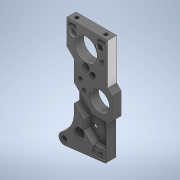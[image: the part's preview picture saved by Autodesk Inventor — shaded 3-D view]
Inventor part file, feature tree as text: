
AUTODESK INVENTOR PART (.ipt)
format: ipt  version: 2022 (Build 260153000, 153)  size: 579,072 bytes
history: native  units: mm
features: extrude x16, sketch x11, fillet x5, projected_geometry x5, thread x2, chamfer x1
ambient origin geometry x8: Origin, YZ Plane, XZ Plane, XY Plane, X Axis, Y Axis, Z Axis, Center Point
bodies: Solid1 (feature_tree)
feature tree (40):
  extrude  "Extrusion1"  Depth=6.0mm
  fillet  "Fillet1"  Radius=23.5mm
  fillet  "Fillet2"  Radius=6.0mm
  extrude  "Extrusion2"  Depth=3.0mm
  extrude  "Extrusion3"  Depth=56.0mm
  thread  "Thread1"  [1 undecoded]
  thread  "Thread2"  [1 undecoded]
  sketch  "Sketch5"  dims[d4=0.0mm d5=3.0mm]
  extrude  "Extrusion4"  Depth=12.5mm
  extrude  "Extrusion5"  Depth=2.1mm
  extrude  "Extrusion6"  Depth=4.0mm
  extrude  "Extrusion7"  TaperAngle=45.0deg  [1 undecoded]
  extrude  "Extrusion8"  Depth=12.0mm
  extrude  "Extrusion9"  TaperAngle=135.0deg  [1 undecoded]
  extrude  "Extrusion10"  Depth=5.0mm TaperAngle=0.0deg
  fillet  "Fillet3"  Radius=3.0mm
  extrude  "Extrusion11"  Depth=10.0mm
  chamfer  "Chamfer1"  Distance=2.5mm
  fillet  "Fillet4"  Radius=13.5mm
  extrude  "Extrusion12"  Depth=10.0mm
  extrude  "Extrusion13"  Depth=10.0mm
  extrude  "Extrusion14"  Depth=10.0mm
  fillet  "Fillet5"  Radius=12.5mm
  extrude  "Extrusion15"  Depth=10.0mm
  extrude  "Extrusion16"  Depth=10.0mm
  sketch  "Sketch3"  dims[d0=3.0mm d1=6.0mm d2=23.5mm d3=6.0mm]
  projected_geometry  "Projected Loop1"
  sketch  "Sketch7"  dims[d6=18.0mm d7=56.0mm d8=11.0mm d9=4.0mm]
  sketch  "Sketch8"  dims[d10=24.75mm d11=12.5mm]
  projected_geometry  "Projected Loop2"
  sketch  "Sketch10"  dims[d12=22.3mm d14=2.1mm]
  sketch  "Sketch13"  dims[d18=30.0mm d20=360.0deg d22=4.0mm]
  sketch  "Sketch15"  dims[d23=14.0mm d24=45.0deg]
  sketch  "Sketch17"  dims[d25=3.0mm d26=12.0mm]
  projected_geometry  "Projected Loop3"
  sketch  "Sketch21"  dims[d27=6.0mm d28=135.0deg]
  projected_geometry  "Projected Loop5"
  sketch  "Sketch22"  dims[d29=135.0deg d30=5.0mm d31=0.0mm d32=3.0mm]
  projected_geometry  "Projected Loop6"
  sketch  "Sketch24"  dims[d33=10.0mm d34=3.0mm d35=2.5mm d36=13.5mm d37=7.5mm d38=2.5mm d39=15.0mm d40=12.5mm d41=1.0mm d42=15.0mm d43=12.75mm d44=20.0mm d45=23.75mm d46=3.0mm d47=0.0mm d48=2.0mm d49=2.0mm d50=2.5mm d51=2.5mm d52=3.0mm d53=3.0mm d54=4.5mm d55=0.0mm d56=7.0mm d57=0.0mm d58=7.0mm d59=0.0mm d60=8.5mm d61=270.0deg d62=4.0mm d63=4.0mm d64=4.0mm d65=3.0mm d66=0.0mm d67=5.5mm d68=2.0mm d69=0.0mm d70=4.0mm d71=1.85mm d72=4.0mm d73=1.85mm d74=1.0mm d75=2.425mm d76=2.425mm d77=1.0mm d78=10.0mm d79=0.0mm d82=3.1mm d83=11.15mm d84=2.1mm d85=2.1mm d86=2.1mm d87=5.5mm d88=3.5mm d89=25.75mm d90=30.25mm d91=2.5mm d92=11.75mm d93=24.0mm d94=8.0mm d95=2.1mm d96=2.1mm d98=2.1mm d99=1.8mm d100=0.0mm d101=2.1mm d102=2.1mm d103=2.1mm d104=1.8mm d105=0.0mm d117=3.9mm d118=0.0mm d119=18.0mm d120=6.5mm d121=0.0mm d122=1.0mm d125=5.0mm d126=7.25mm d127=2.5mm d128=5.0mm d129=15.0mm d130=5.0mm d131=5.0mm d132=90.0deg d133=135.0deg d135=135.0deg d136=135.0deg d137=3.0mm d138=0.0mm d139=0.9mm d140=2.0mm d141=45.0deg d142=4.0mm d143=2.0mm d144=2.6mm d145=3.625mm d146=10.0mm d147=0.0mm d148=2.05mm d149=2.4mm d150=0.0mm d151=4.5mm d154=1.0mm d155=0.0mm d156=2.0mm d157=2.8mm d158=0.5mm d159=10.0mm d160=0.0mm d161=2.5mm d162=0.0mm d80=0.5mm d81=0.872665mm d106=0.872665mm d123=0.872665mm d134=0.5mm d153=0.5mm]
note: 4 required parameter values undecoded (feature->parameter linkage not recoverable at this tier; creation-order binding heuristic only, values carry confidence <= 0.55)
